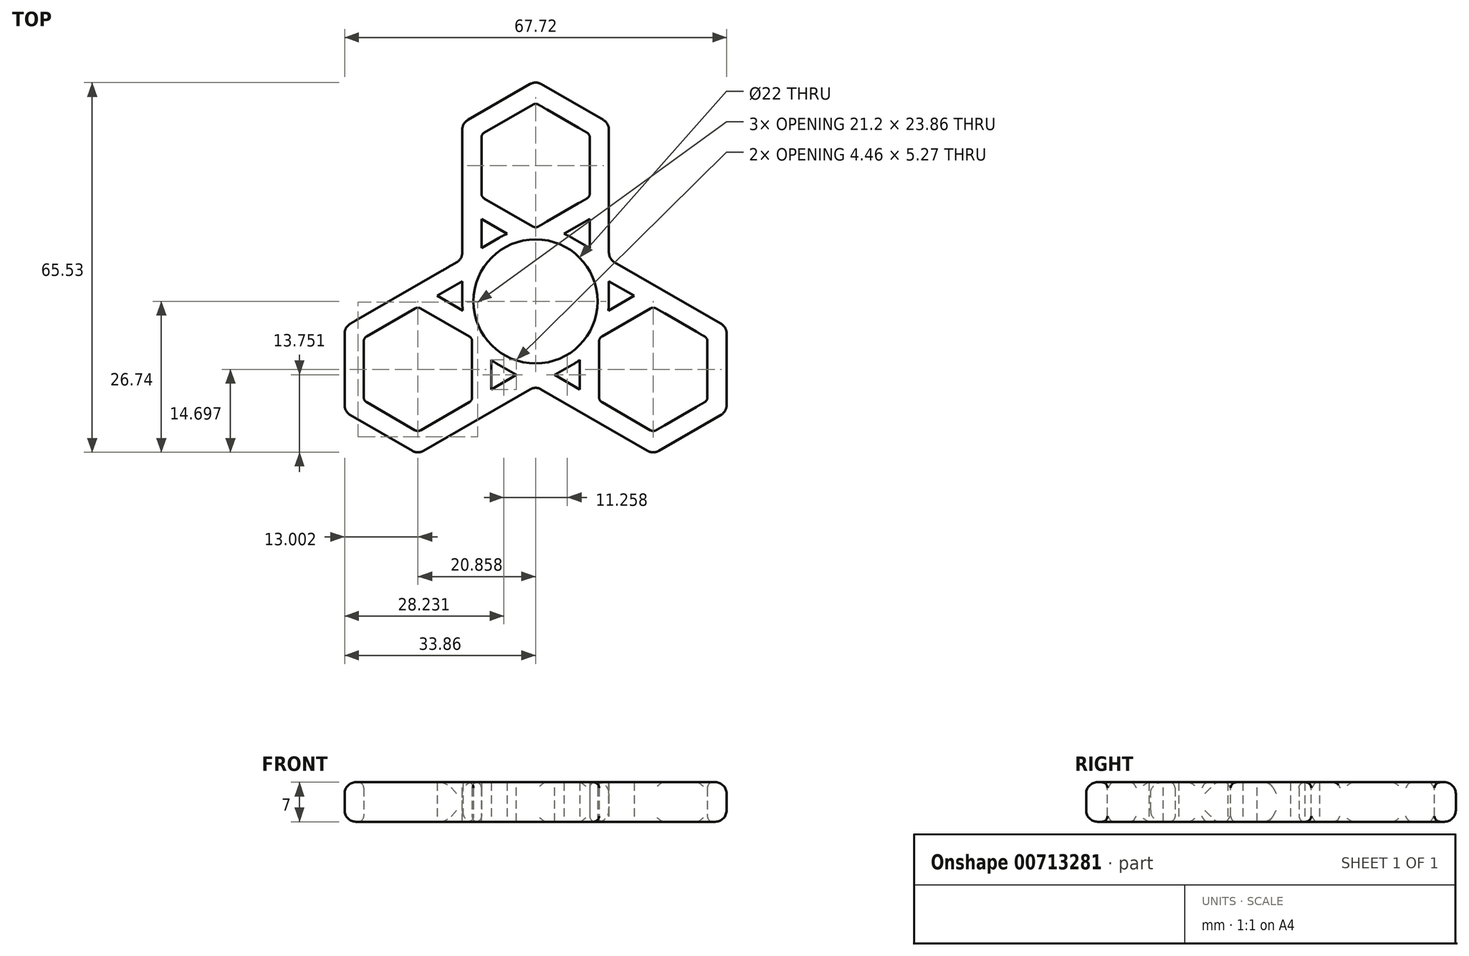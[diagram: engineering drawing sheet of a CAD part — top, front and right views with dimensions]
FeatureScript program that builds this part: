
annotation { "Feature Type Name" : "Feature", "Feature Type Description" : "" }
export const myFeature = defineFeature(function(context is Context, id is Id, definition is map)
    precondition{}
    {
        {
            var Q0;
            Q0=qCreatedBy(makeId("Top.planeOp"),FACE);
            var sketch = newSketch(context, id + "F0", { "sketchPlane" : qUnion([Q0])});
            skCircle(sketch, "E0", {"center": v(0, 24.09) * mm, "radius": 9.6 * mm});
            skCircle(sketch, "E1.cCircle", {"center": v(0, 24.09) * mm, "radius": 9.6 * mm, "construction": true});
            skLineSegment(sketch, "E1.0", {"start": v(0, 35.17) * mm, "end": v(9.6, 29.63) * mm});
            skLineSegment(sketch, "E1.1", {"start": v(9.6, 29.63) * mm, "end": v(9.6, 18.54) * mm});
            skLineSegment(sketch, "E1.2", {"start": v(9.6, 18.54) * mm, "end": v(0, 13) * mm});
            skLineSegment(sketch, "E1.3", {"start": v(0, 13) * mm, "end": v(-9.6, 18.54) * mm});
            skLineSegment(sketch, "E1.4", {"start": v(-9.6, 18.54) * mm, "end": v(-9.6, 29.63) * mm});
            skLineSegment(sketch, "E1.5", {"start": v(-9.6, 29.63) * mm, "end": v(0, 35.17) * mm});
            skPoint(sketch, "E1.0.midPoint", {"position": v(4.8, 32.4) * mm});
            skArc(sketch, "E2", {"start": v(-9.6, 5.37) * mm, "mid": v(0, -11) * mm, "end": v(9.6, 5.37) * mm});
            skArc(sketch, "E3", {"start": v(9.6, 5.37) * mm, "mid": v(0, 11) * mm, "end": v(-9.6, 5.37) * mm});
            skCircle(sketch, "E4", {"center": v(0, 0) * mm, "radius": 13 * mm});
            skLineSegment(sketch, "E5.0", {"start": v(-5.04, 11.98) * mm, "end": v(-13, 16.58) * mm});
            skLineSegment(sketch, "E5.1", {"start": v(-13, 31.6) * mm, "end": v(0, 39.1) * mm});
            skLineSegment(sketch, "E5.2", {"start": v(0, 39.1) * mm, "end": v(13, 31.6) * mm});
            skLineSegment(sketch, "E5.3", {"start": v(-13, 16.58) * mm, "end": v(-13, 31.6) * mm});
            skLineSegment(sketch, "E5.4", {"start": v(13, 31.6) * mm, "end": v(13, 16.58) * mm});
            skLineSegment(sketch, "E5.5", {"start": v(13, 16.58) * mm, "end": v(5.04, 11.98) * mm});
            skLineSegment(sketch, "E6", {"start": v(-13, 16.58) * mm, "end": v(-13, 0) * mm});
            skLineSegment(sketch, "E7", {"start": v(13, 16.58) * mm, "end": v(13, 0) * mm});
            skLineSegment(sketch, "E8", {"start": v(-9.6, 14.62) * mm, "end": v(-9.6, 8.77) * mm});
            skLineSegment(sketch, "E9", {"start": v(9.6, 14.62) * mm, "end": v(9.6, 8.77) * mm});
            skSolve(sketch);
        }
        {
            var Q0;
            {var subQ6=sQuery(id+"F0.wireOp",EDGE,"iIlex7AQ-DfLo-xqRu-M02R-SrluNreQxq9N");Q0=makeQuery(id+"F0.imprint","IMPRINT",FACE,{"disambiguationData":[TD([[makeQuery(id+"F0.imprint","IMPRINT",EDGE,{"derivedFrom":subQ6}),-1.0]])]});}
            var Q1;
            {var subQ5=sQuery(id+"F0.wireOp",EDGE,"E2");Q1=makeQuery(id+"F0.imprint","IMPRINT",FACE,{"disambiguationData":[TD([[makeQuery(id+"F0.imprint","IMPRINT",EDGE,{"derivedFrom":subQ5}),-1.0]])]});}
            var Q2;
            {var subQ0=sQuery(id+"F0.wireOp",EDGE,"E3");Q2=makeQuery(id+"F0.imprint","IMPRINT",FACE,{"disambiguationData":[TD([[makeQuery(id+"F0.imprint","IMPRINT",EDGE,{"derivedFrom":subQ0}),-1.0]])]});}
            var Q3;
            {var subQ11=sQuery(id+"F0.wireOp",EDGE,"33c282a8-e685-4d7a-8cfc-35964cd9419c.0");Q3=makeQuery(id+"F0.imprint","IMPRINT",FACE,{"disambiguationData":[TD([[makeQuery(id+"F0.imprint","IMPRINT",EDGE,{"derivedFrom":subQ11}),-1.0]])]});}
            var Q4;
            {var subQ0=sQuery(id+"F0.wireOp",EDGE,"E6");Q4=makeQuery(id+"F0.imprint","IMPRINT",FACE,{"disambiguationData":[TD([[makeQuery(id+"F0.imprint","IMPRINT",EDGE,{"derivedFrom":subQ0}),1.0]])]});}
            var Q5;
            Q5=makeQuery(id+"F0.imprint","IMPRINT",FACE,{"disambiguationData":[TD([[makeQuery(id+"F0.imprint","IMPRINT",EDGE,{"derivedFrom":sQuery(id+"F0.wireOp",EDGE,"E5.1")}),-1.0]])]});
            var Q6;
            {var subQ0=sQuery(id+"F0.wireOp",EDGE,"E7");Q6=makeQuery(id+"F0.imprint","IMPRINT",FACE,{"disambiguationData":[TD([[makeQuery(id+"F0.imprint","IMPRINT",EDGE,{"derivedFrom":subQ0}),-1.0]])]});}
            extrude(context, id + "F1", {"entities" : qUnion([Q0, Q1, Q2, Q3, Q4, Q5, Q6]), "depth" : 7 * mm, "offsetDistance" : 25 * mm});
        }
        {
            var Q0;
            Q0=makeQuery(id+"F1.opExtrude","SWEPT_BODY",BODY,{"disambiguationData":[OSD([sQuery(id+"F0.wireOp",EDGE,"E1.0"),sQuery(id+"F0.wireOp",EDGE,"E1.1"),sQuery(id+"F0.wireOp",EDGE,"E1.2"),sQuery(id+"F0.wireOp",EDGE,"E1.3"),sQuery(id+"F0.wireOp",EDGE,"E1.4"),sQuery(id+"F0.wireOp",EDGE,"E1.5"),sQuery(id+"F0.wireOp",EDGE,"iIlex7AQ-DfLo-xqRu-M02R-SrluNreQxq9N"),sQuery(id+"F0.wireOp",EDGE,"WDQDbg9l-taql-AzW7-Nxgt-qL86zbRJRPn5"),sQuery(id+"F0.wireOp",EDGE,"E2"),sQuery(id+"F0.wireOp",EDGE,"E3"),sQuery(id+"F0.wireOp",EDGE,"97b70cb2-d818-4921-8de6-4375d2823b8e.0"),sQuery(id+"F0.wireOp",EDGE,"97b70cb2-d818-4921-8de6-4375d2823b8e.1"),sQuery(id+"F0.wireOp",EDGE,"97b70cb2-d818-4921-8de6-4375d2823b8e.2"),sQuery(id+"F0.wireOp",EDGE,"97b70cb2-d818-4921-8de6-4375d2823b8e.3"),sQuery(id+"F0.wireOp",EDGE,"97b70cb2-d818-4921-8de6-4375d2823b8e.4"),sQuery(id+"F0.wireOp",EDGE,"97b70cb2-d818-4921-8de6-4375d2823b8e.5"),sQuery(id+"F0.wireOp",EDGE,"a09d1221-abeb-479f-9bc4-481f7c2af454.0"),sQuery(id+"F0.wireOp",EDGE,"ba5f16a2-e924-401b-b4b4-8cdbce717970"),sQuery(id+"F0.wireOp",EDGE,"33c282a8-e685-4d7a-8cfc-35964cd9419c.0"),sQuery(id+"F0.wireOp",EDGE,"32758f72-db0b-44e0-a302-32a3ce6b2c94.0")])]});
            var Q1;
            Q1=makeQuery(id+"F1.opExtrude","CAP_EDGE",EDGE,{"disambiguationData":[OSD([sQuery(id+"F0.wireOp",EDGE,"E2"),sQuery(id+"F0.wireOp",EDGE,"E3")])],"isStart":false});
            circularPattern(context, id + "F2", {"operationType" : NewBodyOperationType.ADD, "entities" : qUnion([Q0]), "axis" : qUnion([Q1]), "angle" : 360 * degree, "instanceCount" : 3, "equalSpace" : true});
        }
        {
            var Q0;
            Q0=makeQuery(id+"F2.opPattern","COPY",FACE,{"derivedFrom":makeQuery(id+"F1.opExtrude","SWEPT_FACE",FACE,{"disambiguationData":[OSD([sQuery(id+"F0.wireOp",EDGE,"E5.2")])]}),"instanceName":"1"});
            var Q1;
            Q1=makeQuery(id+"F2.opPattern","COPY",FACE,{"derivedFrom":makeQuery(id+"F1.opExtrude","SWEPT_FACE",FACE,{"disambiguationData":[OSD([sQuery(id+"F0.wireOp",EDGE,"E5.1")])]}),"instanceName":"1"});
            var Q2;
            {var subQ3=sQuery(id+"F0.wireOp",EDGE,"E6");var subQ6=sQuery(id+"F0.wireOp",EDGE,"E5.3");var subQ8=sQuery(id+"F0.wireOp",EDGE,"E5.1");Q2=makeQuery(id+"F2.boolean.opBoolean","SPLIT",FACE,{"disambiguationData":[TD([makeQuery(id+"F2.opPattern","COPY",FACE,{"derivedFrom":makeQuery(id+"F1.opExtrude","SWEPT_FACE",FACE,{"disambiguationData":[OSD([subQ8])]}),"instanceName":"1"})])],"derivedFrom":makeQuery(id+"F2.opPattern","COPY",FACE,{"derivedFrom":makeQuery(id+"F1.opExtrude","SWEPT_FACE",FACE,{"disambiguationData":[OSD([subQ6,subQ3])]}),"instanceName":"1"})});}
            var Q3;
            {var subQ2=sQuery(id+"F0.wireOp",EDGE,"E7");var subQ5=sQuery(id+"F0.wireOp",EDGE,"E5.4");var subQ7=sQuery(id+"F0.wireOp",EDGE,"E5.2");Q3=makeQuery(id+"F2.boolean.opBoolean","SPLIT",FACE,{"disambiguationData":[TD([makeQuery(id+"F2.opPattern","COPY",FACE,{"derivedFrom":makeQuery(id+"F1.opExtrude","SWEPT_FACE",FACE,{"disambiguationData":[OSD([subQ7])]}),"instanceName":"2"})])],"derivedFrom":makeQuery(id+"F2.opPattern","COPY",FACE,{"derivedFrom":makeQuery(id+"F1.opExtrude","SWEPT_FACE",FACE,{"disambiguationData":[OSD([subQ5,subQ2])]}),"instanceName":"2"})});}
            var Q4;
            Q4=makeQuery(id+"F2.opPattern","COPY",FACE,{"derivedFrom":makeQuery(id+"F1.opExtrude","SWEPT_FACE",FACE,{"disambiguationData":[OSD([sQuery(id+"F0.wireOp",EDGE,"E5.2")])]}),"instanceName":"2"});
            var Q5;
            Q5=makeQuery(id+"F2.opPattern","COPY",FACE,{"derivedFrom":makeQuery(id+"F1.opExtrude","SWEPT_FACE",FACE,{"disambiguationData":[OSD([sQuery(id+"F0.wireOp",EDGE,"E5.1")])]}),"instanceName":"2"});
            var Q6;
            {var subQ3=sQuery(id+"F0.wireOp",EDGE,"E6");var subQ6=sQuery(id+"F0.wireOp",EDGE,"E5.3");var subQ8=sQuery(id+"F0.wireOp",EDGE,"E5.1");Q6=makeQuery(id+"F2.boolean.opBoolean","SPLIT",FACE,{"disambiguationData":[TD([makeQuery(id+"F2.opPattern","COPY",FACE,{"derivedFrom":makeQuery(id+"F1.opExtrude","SWEPT_FACE",FACE,{"disambiguationData":[OSD([subQ8])]}),"instanceName":"2"})])],"derivedFrom":makeQuery(id+"F2.opPattern","COPY",FACE,{"derivedFrom":makeQuery(id+"F1.opExtrude","SWEPT_FACE",FACE,{"disambiguationData":[OSD([subQ6,subQ3])]}),"instanceName":"2"})});}
            var Q7;
            {var subQ0=sQuery(id+"F0.wireOp",EDGE,"E5.2");var subQ3=sQuery(id+"F0.wireOp",EDGE,"E7");var subQ6=sQuery(id+"F0.wireOp",EDGE,"E5.4");Q7=makeQuery(id+"F2.boolean.opBoolean","SPLIT",FACE,{"disambiguationData":[TD([makeQuery(id+"F1.opExtrude","SWEPT_FACE",FACE,{"disambiguationData":[OSD([subQ0])]})])],"derivedFrom":makeQuery(id+"F1.opExtrude","SWEPT_FACE",FACE,{"disambiguationData":[OSD([subQ6,subQ3])]})});}
            var Q8;
            Q8=makeQuery(id+"F1.opExtrude","SWEPT_FACE",FACE,{"disambiguationData":[OSD([sQuery(id+"F0.wireOp",EDGE,"E5.2")])]});
            var Q9;
            Q9=makeQuery(id+"F1.opExtrude","SWEPT_FACE",FACE,{"disambiguationData":[OSD([sQuery(id+"F0.wireOp",EDGE,"E5.1")])]});
            var Q10;
            {var subQ0=sQuery(id+"F0.wireOp",EDGE,"E5.1");var subQ4=sQuery(id+"F0.wireOp",EDGE,"E6");var subQ7=sQuery(id+"F0.wireOp",EDGE,"E5.3");Q10=makeQuery(id+"F2.boolean.opBoolean","SPLIT",FACE,{"disambiguationData":[TD([makeQuery(id+"F1.opExtrude","SWEPT_FACE",FACE,{"disambiguationData":[OSD([subQ0])]})])],"derivedFrom":makeQuery(id+"F1.opExtrude","SWEPT_FACE",FACE,{"disambiguationData":[OSD([subQ7,subQ4])]})});}
            fillet(context, id + "F3", {"entities" : qUnion([Q0, Q1, Q2, Q3, Q4, Q5, Q6, Q7, Q8, Q9, Q10]), "radius" : 2 * mm, "tangentPropagation" : true, "allowEdgeOverflow" : false});
        }
        {
            var Q0;
            Q0=makeQuery(id+"F1.opExtrude","CAP_EDGE",EDGE,{"disambiguationData":[OSD([sQuery(id+"F0.wireOp",EDGE,"E2"),sQuery(id+"F0.wireOp",EDGE,"E3")])],"isStart":false});
            var Q1;
            Q1=makeQuery(id+"F1.opExtrude","CAP_EDGE",EDGE,{"disambiguationData":[OSD([sQuery(id+"F0.wireOp",EDGE,"E2"),sQuery(id+"F0.wireOp",EDGE,"E3")])],"isStart":true});
            var Q2;
            Q2=makeQuery(id+"F2.opPattern","COPY",FACE,{"derivedFrom":makeQuery(id+"F1.opExtrude","SWEPT_FACE",FACE,{"disambiguationData":[OSD([sQuery(id+"F0.wireOp",EDGE,"E1.2")])]}),"instanceName":"1"});
            var Q3;
            Q3=makeQuery(id+"F2.opPattern","COPY",FACE,{"derivedFrom":makeQuery(id+"F1.opExtrude","SWEPT_FACE",FACE,{"disambiguationData":[OSD([sQuery(id+"F0.wireOp",EDGE,"E1.1")])]}),"instanceName":"1"});
            var Q4;
            Q4=makeQuery(id+"F2.opPattern","COPY",FACE,{"derivedFrom":makeQuery(id+"F1.opExtrude","SWEPT_FACE",FACE,{"disambiguationData":[OSD([sQuery(id+"F0.wireOp",EDGE,"E1.0")])]}),"instanceName":"1"});
            var Q5;
            Q5=makeQuery(id+"F2.opPattern","COPY",FACE,{"derivedFrom":makeQuery(id+"F1.opExtrude","SWEPT_FACE",FACE,{"disambiguationData":[OSD([sQuery(id+"F0.wireOp",EDGE,"E1.4")])]}),"instanceName":"1"});
            var Q6;
            Q6=makeQuery(id+"F2.opPattern","COPY",FACE,{"derivedFrom":makeQuery(id+"F1.opExtrude","SWEPT_FACE",FACE,{"disambiguationData":[OSD([sQuery(id+"F0.wireOp",EDGE,"E1.3")])]}),"instanceName":"1"});
            var Q7;
            Q7=makeQuery(id+"F2.opPattern","COPY",FACE,{"derivedFrom":makeQuery(id+"F1.opExtrude","SWEPT_FACE",FACE,{"disambiguationData":[OSD([sQuery(id+"F0.wireOp",EDGE,"E1.5")])]}),"instanceName":"1"});
            var Q8;
            Q8=makeQuery(id+"F1.opExtrude","SWEPT_FACE",FACE,{"disambiguationData":[OSD([sQuery(id+"F0.wireOp",EDGE,"E1.3")])]});
            var Q9;
            Q9=makeQuery(id+"F1.opExtrude","SWEPT_FACE",FACE,{"disambiguationData":[OSD([sQuery(id+"F0.wireOp",EDGE,"E1.1")])]});
            var Q10;
            Q10=makeQuery(id+"F1.opExtrude","SWEPT_FACE",FACE,{"disambiguationData":[OSD([sQuery(id+"F0.wireOp",EDGE,"E1.5")])]});
            var Q11;
            Q11=makeQuery(id+"F2.opPattern","COPY",FACE,{"derivedFrom":makeQuery(id+"F1.opExtrude","SWEPT_FACE",FACE,{"disambiguationData":[OSD([sQuery(id+"F0.wireOp",EDGE,"E1.1")])]}),"instanceName":"2"});
            var Q12;
            Q12=makeQuery(id+"F2.opPattern","COPY",FACE,{"derivedFrom":makeQuery(id+"F1.opExtrude","SWEPT_FACE",FACE,{"disambiguationData":[OSD([sQuery(id+"F0.wireOp",EDGE,"E1.5")])]}),"instanceName":"2"});
            var Q13;
            Q13=makeQuery(id+"F2.opPattern","COPY",FACE,{"derivedFrom":makeQuery(id+"F1.opExtrude","SWEPT_FACE",FACE,{"disambiguationData":[OSD([sQuery(id+"F0.wireOp",EDGE,"E1.3")])]}),"instanceName":"2"});
            fillet(context, id + "F4", {"entities" : qUnion([Q0, Q1, Q2, Q3, Q4, Q5, Q6, Q7, Q8, Q9, Q10, Q11, Q12, Q13]), "radius" : 1 * mm, "tangentPropagation" : true, "allowEdgeOverflow" : false});
        }
    });
